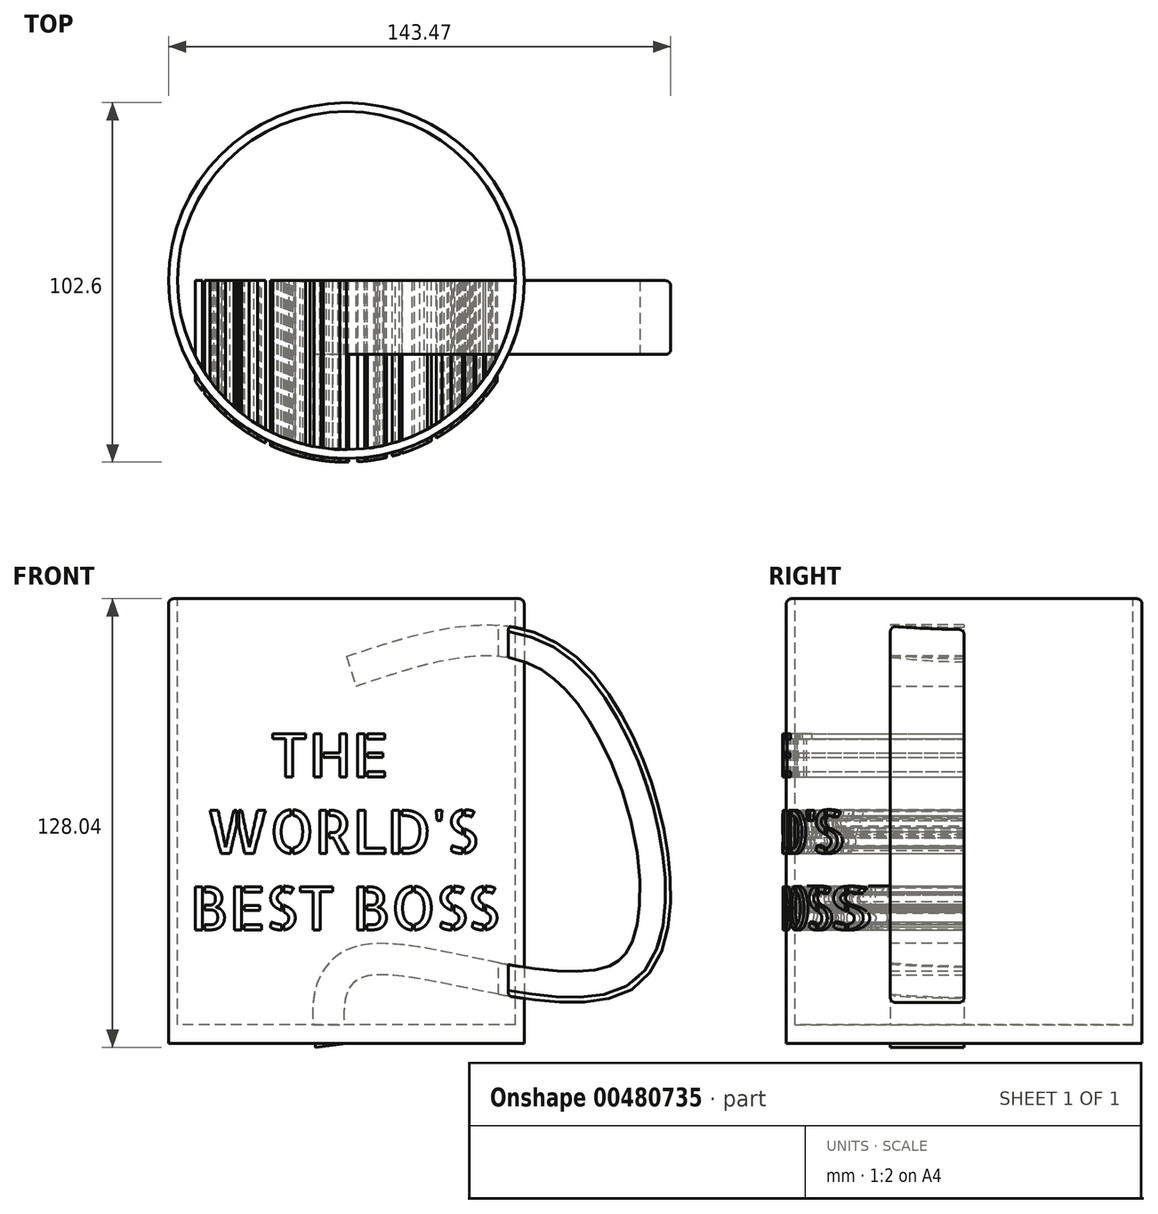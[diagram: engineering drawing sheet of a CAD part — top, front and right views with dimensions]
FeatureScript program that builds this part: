
annotation { "Feature Type Name" : "Feature", "Feature Type Description" : "" }
export const myFeature = defineFeature(function(context is Context, id is Id, definition is map)
    precondition{}
    {
        {
            var Q0;
            Q0=qCreatedBy(makeId("Top.planeOp"),FACE);
            var sketch = newSketch(context, id + "F0", { "sketchPlane" : qUnion([Q0])});
            skCircle(sketch, "E0", {"center": v(0, 0) * mm, "radius": 50.8 * mm});
            skSolve(sketch);
        }
        {
            var Q0;
            Q0 = qSketchRegion(id + "F0", true);
            extrude(context, id + "F1", {"entities" : qUnion([Q0]), "depth" : 127 * mm});
        }
        {
            var Q0;
            Q0=makeQuery(id+"F1.opExtrude","CAP_FACE",FACE,{"disambiguationData":[OSD([sQuery(id+"F0.wireOp",EDGE,"E0")])],"isStart":false});
            var sketch = newSketch(context, id + "F2", { "sketchPlane" : qUnion([Q0])});
            skCircle(sketch, "E1", {"center": v(0, 0) * mm, "radius": 48.26 * mm});
            skSolve(sketch);
        }
        {
            var Q0;
            Q0 = qSketchRegion(id + "F2", true);
            extrude(context, id + "F3", {"entities" : qUnion([Q0]), "operationType" : NewBodyOperationType.REMOVE, "oppositeDirection" : true, "depth" : 121.67 * mm});
        }
        {
            var Q0;
            Q0=qCreatedBy(makeId("Front.planeOp"),FACE);
            var sketch = newSketch(context, id + "F4", { "sketchPlane" : qUnion([Q0])});
            skText(sketch, "E2", { "text": "     THE \n WORLD\'S \nBEST BOSS", "fontName": "AllertaStencil-Regular.ttf"});
            const initialGuessF4  = {"E2": [-0.0447, 0.07615, 1, 0, 0.01228]};
            skSetInitialGuess(sketch, initialGuessF4);
            skSolve(sketch);
        }
        {
            var Q0;
            Q0 = qSketchRegion(id + "F4", true);
            extrude(context, id + "F5", {"entities" : qUnion([Q0]), "operationType" : NewBodyOperationType.ADD, "depth" : 63.5 * mm});
        }
        {
            var Q0;
            Q0=qCreatedBy(makeId("Front.planeOp"),FACE);
            var sketch = newSketch(context, id + "F6", { "sketchPlane" : qUnion([Q0])});
            skLineSegment(sketch, "E3", {"start": v(0, 0) * mm, "end": v(0, 151.77) * mm, "construction": true});
            skSolve(sketch);
        }
        {
            var Q0;
            Q0=qCreatedBy(makeId("Front.planeOp"),FACE);
            var sketch = newSketch(context, id + "F7", { "sketchPlane" : qUnion([Q0])});
            skLineSegment(sketch, "E4", {"start": v(-50.8, 0) * mm, "end": v(-50.8, 127) * mm});
            skLineSegment(sketch, "E5", {"start": v(50.8, 127) * mm, "end": v(50.8, 0) * mm});
            skLineSegment(sketch, "E6.0", {"start": v(-50.8, -1) * mm, "end": v(51.8, -1) * mm});
            skLineSegment(sketch, "E6.1", {"start": v(51.8, 128) * mm, "end": v(51.8, -1) * mm});
            skLineSegment(sketch, "E6.2", {"start": v(-50.8, 128) * mm, "end": v(51.8, 128) * mm});
            skLineSegment(sketch, "E7", {"start": v(16.57, 128) * mm, "end": v(59.32, 144.97) * mm});
            skLineSegment(sketch, "E8", {"start": v(59.32, 144.97) * mm, "end": v(99.1, 49.24) * mm});
            skLineSegment(sketch, "E9", {"start": v(99.1, 49.24) * mm, "end": v(62.01, -32.22) * mm});
            skLineSegment(sketch, "E10", {"start": v(62.01, -32.22) * mm, "end": v(35.54, -32.22) * mm});
            skLineSegment(sketch, "E11", {"start": v(35.54, -32.22) * mm, "end": v(29.23, -1) * mm});
            skSolve(sketch);
        }
        {
            var Q0;
            Q0 = qSketchRegion(id + "F7", true);
            var Q1;
            Q1=sQuery(id+"F6.wireOp",EDGE,"E3");
            revolve(context, id + "F8", {"operationType" : NewBodyOperationType.REMOVE, "entities" : qUnion([Q0]), "axis" : qUnion([Q1]), "revolveType" : RevolveType.FULL, "oppositeDirection" : true});
        }
        {
            var Q0;
            Q0=qCreatedBy(makeId("Front.planeOp"),FACE);
            var sketch = newSketch(context, id + "F9", { "sketchPlane" : qUnion([Q0])});
            skFitSpline(sketch, "E12", {"points": [v(0, 110.54) * mm, v(67.25, 109) * mm, v(83.14, 16.58) * mm, v(5.09, 19.07) * mm, v(0, 0) * mm], "startDerivative": vector(277.66, 91.56) * mm, "endDerivative": vector(20.88, -177.97) * mm});
            skFitSpline(sketch, "E13.0", {"points": [v(2.78, 102.1) * mm, v(5.68, 103.05) * mm, v(11.4, 104.93) * mm, v(19.69, 107.43) * mm, v(27.61, 109.38) * mm, v(35.05, 110.54) * mm, v(41.88, 110.77) * mm, v(47.01, 110.1) * mm, v(50.83, 109) * mm, v(53.59, 107.87) * mm, v(56.27, 106.41) * mm, v(58.47, 104.87) * mm, v(60.23, 103.4) * mm, v(61.98, 101.77) * mm, v(64.2, 99.38) * mm, v(66.84, 95.97) * mm, v(69.42, 92.1) * mm, v(71.87, 87.84) * mm, v(74.94, 81.72) * mm, v(78.3, 73.43) * mm, v(81.38, 63) * mm, v(83.33, 52.65) * mm, v(83.88, 44.57) * mm, v(83.67, 38.75) * mm, v(83.18, 34.8) * mm, v(82.39, 31.33) * mm, v(81.34, 28.43) * mm, v(80.31, 26.54) * mm, v(79.44, 25.32) * mm, v(78.76, 24.54) * mm, v(78.06, 23.88) * mm, v(77.34, 23.33) * mm, v(76.48, 22.8) * mm, v(75.14, 22.16) * mm, v(73.08, 21.46) * mm, v(69.98, 20.88) * mm, v(66.33, 20.6) * mm, v(62.23, 20.63) * mm, v(57.8, 20.95) * mm, v(51.54, 21.7) * mm, v(43.29, 23.12) * mm, v(34.94, 24.84) * mm, v(28.44, 26.16) * mm, v(23.7, 27.07) * mm, v(19.13, 27.83) * mm, v(15.47, 28.29) * mm, v(12.61, 28.5) * mm, v(10.5, 28.58) * mm, v(8.4, 28.55) * mm, v(6.64, 28.41) * mm, v(5.22, 28.21) * mm, v(4.14, 28.01) * mm, v(3.05, 27.75) * mm, v(1.57, 27.3) * mm, v(-0.24, 26.55) * mm, v(-2.28, 25.35) * mm, v(-4.12, 23.86) * mm, v(-5.67, 22.15) * mm, v(-6.92, 20.32) * mm, v(-7.86, 18.44) * mm, v(-8.55, 16.57) * mm, v(-9.18, 14.14) * mm, v(-9.55, 11.24) * mm, v(-9.62, 7.96) * mm, v(-9.45, 4.82) * mm, v(-9.16, 1.8) * mm, v(-8.94, -0.1) * mm, v(-8.83, -1.04) * mm]});
            skLineSegment(sketch, "E14", {"start": v(0, 110.54) * mm, "end": v(2.78, 102.1) * mm});
            skLineSegment(sketch, "E15", {"start": v(-8.83, -1.04) * mm, "end": v(0, 0) * mm});
            skSolve(sketch);
        }
        {
            var Q0;
            Q0 = qSketchRegion(id + "F9", true);
            extrude(context, id + "F10", {"entities" : qUnion([Q0]), "operationType" : NewBodyOperationType.ADD, "depth" : 21.08 * mm});
        }
        {
            var Q0;
            {var subQ0=sQuery(id+"F9.wireOp",EDGE,"E12");Q0=makeQuery(id+"F10.boolean.opBoolean","SPLIT",EDGE,{"disambiguationData":[TD([makeQuery(id+"F1.opExtrude","SWEPT_FACE",FACE,{"disambiguationData":[OSD([sQuery(id+"F0.wireOp",EDGE,"E0")])]})])],"derivedFrom":makeQuery(id+"F10.opExtrude","CAP_EDGE",EDGE,{"disambiguationData":[OSD([subQ0])],"isStart":false})});}
            var Q1;
            {var subQ0=sQuery(id+"F9.wireOp",EDGE,"E12");Q1=makeQuery(id+"F10.boolean.opBoolean","SPLIT",EDGE,{"disambiguationData":[TD([makeQuery(id+"F1.opExtrude","SWEPT_FACE",FACE,{"disambiguationData":[OSD([sQuery(id+"F0.wireOp",EDGE,"E0")])]})])],"derivedFrom":makeQuery(id+"F10.opExtrude","CAP_EDGE",EDGE,{"disambiguationData":[OSD([subQ0])],"isStart":true})});}
            var Q2;
            Q2=makeQuery(id+"F1.opExtrude","CAP_EDGE",EDGE,{"disambiguationData":[OSD([sQuery(id+"F0.wireOp",EDGE,"E0")])],"isStart":false});
            fillet(context, id + "F11", {"entities" : qUnion([Q0, Q1, Q2]), "radius" : 1.5 * mm, "tangentPropagation" : true, "allowEdgeOverflow" : false});
        }
    });
